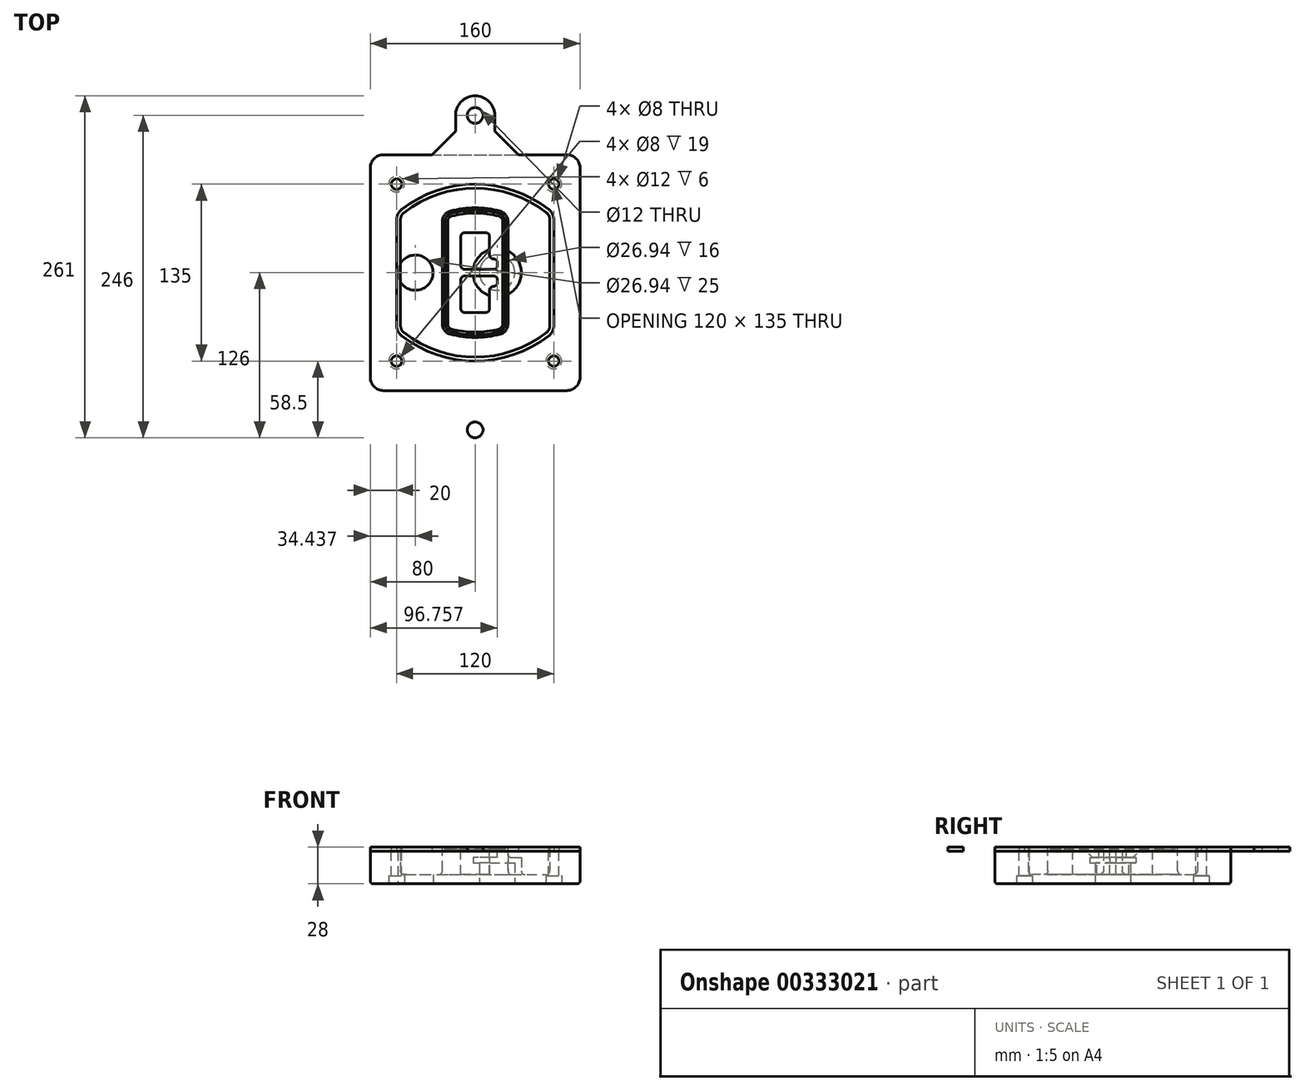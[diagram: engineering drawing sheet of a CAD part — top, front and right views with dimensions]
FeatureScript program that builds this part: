
annotation { "Feature Type Name" : "Feature", "Feature Type Description" : "" }
export const myFeature = defineFeature(function(context is Context, id is Id, definition is map)
    precondition{}
    {
        {
            var Q0;
            Q0=qCreatedBy(makeId("Top.planeOp"),FACE);
            var sketch = newSketch(context, id + "F0", { "sketchPlane" : qUnion([Q0])});
            skPoint(sketch, "E0.rect.middle", {"position": v(0, 0) * mm});
            skLineSegment(sketch, "E1.bottom", {"start": v(-70, -90) * mm, "end": v(70, -90) * mm});
            skLineSegment(sketch, "E1.top", {"start": v(-70, 90) * mm, "end": v(70, 90) * mm});
            skLineSegment(sketch, "E1.left", {"start": v(-80, -80) * mm, "end": v(-80, 80) * mm});
            skLineSegment(sketch, "E1.right", {"start": v(80, -80) * mm, "end": v(80, 80) * mm});
            skLineSegment(sketch, "E2", {"start": v(-80, 90) * mm, "end": v(80, -90) * mm, "construction": true});
            skLineSegment(sketch, "E3", {"start": v(80, 90) * mm, "end": v(-80, -90) * mm, "construction": true});
            skCircle(sketch, "E4", {"center": v(-60, 67.5) * mm, "radius": 4 * mm});
            skCircle(sketch, "E5", {"center": v(60, 67.5) * mm, "radius": 4 * mm});
            skCircle(sketch, "E6", {"center": v(60, -67.5) * mm, "radius": 4 * mm});
            skCircle(sketch, "E7", {"center": v(-60, -67.5) * mm, "radius": 4 * mm});
            skLineSegment(sketch, "E8", {"start": v(-60, 67.5) * mm, "end": v(60, 67.5) * mm, "construction": true});
            skLineSegment(sketch, "E9", {"start": v(60, 67.5) * mm, "end": v(60, -67.5) * mm, "construction": true});
            skLineSegment(sketch, "E10", {"start": v(60, -67.5) * mm, "end": v(-60, -67.5) * mm, "construction": true});
            skLineSegment(sketch, "E11", {"start": v(-60, -67.5) * mm, "end": v(-60, 67.5) * mm, "construction": true});
            skLineSegment(sketch, "E12", {"start": v(-60, 40.3) * mm, "end": v(-60, -40.3) * mm});
            skLineSegment(sketch, "E13", {"start": v(60, 40.3) * mm, "end": v(60, -40.3) * mm});
            skArc(sketch, "E14", {"start": v(56.15, 48.18) * mm, "mid": v(0, 67.5) * mm, "end": v(-56.15, 48.18) * mm});
            skArc(sketch, "E15", {"start": v(-56.15, -48.18) * mm, "mid": v(0, -67.5) * mm, "end": v(56.15, -48.18) * mm});
            skLineSegment(sketch, "E16", {"start": v(-60, 0) * mm, "end": v(60, 0) * mm, "construction": true});
            skPoint(sketch, "E17.visualSharp", {"position": v(-60, -45) * mm});
            skArc(sketch, "E17.filletArc", {"start": v(-60, -40.3) * mm, "mid": v(-58.99, -44.68) * mm, "end": v(-56.15, -48.18) * mm});
            skPoint(sketch, "E18.visualSharp", {"position": v(-60, 45) * mm});
            skArc(sketch, "E18.filletArc", {"start": v(-56.15, 48.18) * mm, "mid": v(-58.99, 44.68) * mm, "end": v(-60, 40.3) * mm});
            skPoint(sketch, "E19.visualSharp", {"position": v(60, 45) * mm});
            skArc(sketch, "E19.filletArc", {"start": v(60, 40.3) * mm, "mid": v(58.99, 44.68) * mm, "end": v(56.15, 48.18) * mm});
            skPoint(sketch, "E20.visualSharp", {"position": v(60, -45) * mm});
            skArc(sketch, "E20.filletArc", {"start": v(56.15, -48.18) * mm, "mid": v(58.99, -44.68) * mm, "end": v(60, -40.3) * mm});
            skPoint(sketch, "E21.visualSharp", {"position": v(-80, 90) * mm});
            skArc(sketch, "E21.filletArc", {"start": v(-70, 90) * mm, "mid": v(-77.07, 87.07) * mm, "end": v(-80, 80) * mm});
            skPoint(sketch, "E22.visualSharp", {"position": v(80, 90) * mm});
            skArc(sketch, "E22.filletArc", {"start": v(80, 80) * mm, "mid": v(77.07, 87.07) * mm, "end": v(70, 90) * mm});
            skPoint(sketch, "E23.visualSharp", {"position": v(80, -90) * mm});
            skArc(sketch, "E23.filletArc", {"start": v(70, -90) * mm, "mid": v(77.07, -87.07) * mm, "end": v(80, -80) * mm});
            skPoint(sketch, "E24.visualSharp", {"position": v(-80, -90) * mm});
            skArc(sketch, "E24.filletArc", {"start": v(-80, -80) * mm, "mid": v(-77.07, -87.07) * mm, "end": v(-70, -90) * mm});
            skArc(sketch, "E25.0", {"start": v(57, 40.3) * mm, "mid": v(56.3, 43.36) * mm, "end": v(54.3, 45.81) * mm});
            skLineSegment(sketch, "E25.1", {"start": v(57, 40.3) * mm, "end": v(57, -40.3) * mm});
            skArc(sketch, "E25.2", {"start": v(54.3, -45.81) * mm, "mid": v(56.3, -43.36) * mm, "end": v(57, -40.3) * mm});
            skArc(sketch, "E25.3", {"start": v(-54.3, -45.81) * mm, "mid": v(0, -64.5) * mm, "end": v(54.3, -45.81) * mm});
            skArc(sketch, "E25.4", {"start": v(-57, -40.3) * mm, "mid": v(-56.3, -43.36) * mm, "end": v(-54.3, -45.81) * mm});
            skArc(sketch, "E25.5", {"start": v(54.3, 45.81) * mm, "mid": v(0, 64.5) * mm, "end": v(-54.3, 45.81) * mm});
            skLineSegment(sketch, "E25.6", {"start": v(-57, 40.3) * mm, "end": v(-57, -40.3) * mm});
            skArc(sketch, "E25.7", {"start": v(-54.3, 45.81) * mm, "mid": v(-56.3, 43.36) * mm, "end": v(-57, 40.3) * mm});
            skArc(sketch, "E26.0", {"start": v(-58.62, 51.33) * mm, "mid": v(-62.58, 46.43) * mm, "end": v(-64, 40.3) * mm});
            skArc(sketch, "E26.1", {"start": v(58.62, 51.33) * mm, "mid": v(0, 71.5) * mm, "end": v(-58.62, 51.33) * mm});
            skArc(sketch, "E26.2", {"start": v(64, 40.3) * mm, "mid": v(62.58, 46.43) * mm, "end": v(58.62, 51.33) * mm});
            skLineSegment(sketch, "E26.3", {"start": v(64, 40.3) * mm, "end": v(64, -40.3) * mm});
            skArc(sketch, "E26.4", {"start": v(58.62, -51.33) * mm, "mid": v(62.58, -46.43) * mm, "end": v(64, -40.3) * mm});
            skLineSegment(sketch, "E26.5", {"start": v(-64, 40.3) * mm, "end": v(-64, -40.3) * mm});
            skArc(sketch, "E26.6", {"start": v(-58.62, -51.33) * mm, "mid": v(0, -71.5) * mm, "end": v(58.62, -51.33) * mm});
            skArc(sketch, "E26.7", {"start": v(-64, -40.3) * mm, "mid": v(-62.58, -46.43) * mm, "end": v(-58.62, -51.33) * mm});
            skSolve(sketch);
        }
        {
            var Q0;
            Q0=makeQuery(id+"F0.imprint","IMPRINT",FACE,{"disambiguationData":[TD([[makeQuery(id+"F0.imprint","IMPRINT",EDGE,{"derivedFrom":sQuery(id+"F0.wireOp",EDGE,"E1.bottom")}),1.0]])]});
            var Q1;
            Q1=makeQuery(id+"F0.imprint","IMPRINT",FACE,{"disambiguationData":[TD([[makeQuery(id+"F0.imprint","IMPRINT",EDGE,{"derivedFrom":sQuery(id+"F0.wireOp",EDGE,"E12")}),1.0]])]});
            var Q2;
            Q2=makeQuery(id+"F0.imprint","IMPRINT",FACE,{"disambiguationData":[TD([[makeQuery(id+"F0.imprint","IMPRINT",EDGE,{"derivedFrom":sQuery(id+"F0.wireOp",EDGE,"E25.0")}),1.0]])]});
            var Q3;
            Q3=makeQuery(id+"F0.imprint","IMPRINT",FACE,{"disambiguationData":[TD([[makeQuery(id+"F0.imprint","IMPRINT",EDGE,{"derivedFrom":sQuery(id+"F0.wireOp",EDGE,"E12")}),-1.0]])]});
            extrude(context, id + "F1", {"entities" : qUnion([Q0, Q1, Q2, Q3]), "oppositeDirection" : true, "depth" : 25 * mm});
        }
        {
            var Q0;
            Q0=makeQuery(id+"F0.imprint","IMPRINT",FACE,{"disambiguationData":[TD([[makeQuery(id+"F0.imprint","IMPRINT",EDGE,{"derivedFrom":sQuery(id+"F0.wireOp",EDGE,"E12")}),1.0]])]});
            extrude(context, id + "F2", {"entities" : qUnion([Q0]), "operationType" : NewBodyOperationType.ADD, "depth" : 3 * mm});
        }
        {
            var Q0;
            Q0=makeQuery(id+"F0.imprint","IMPRINT",FACE,{"disambiguationData":[TD([[makeQuery(id+"F0.imprint","IMPRINT",EDGE,{"derivedFrom":sQuery(id+"F0.wireOp",EDGE,"E25.0")}),1.0]])]});
            extrude(context, id + "F3", {"entities" : qUnion([Q0]), "operationType" : NewBodyOperationType.REMOVE, "oppositeDirection" : true, "depth" : 18 * mm});
        }
        {
            var Q0;
            Q0=makeQuery(id+"F2.opExtrude","CAP_FACE",FACE,{"disambiguationData":[OSD([sQuery(id+"F0.wireOp",EDGE,"E12"),sQuery(id+"F0.wireOp",EDGE,"E13"),sQuery(id+"F0.wireOp",EDGE,"E14"),sQuery(id+"F0.wireOp",EDGE,"E15"),sQuery(id+"F0.wireOp",EDGE,"E17.filletArc"),sQuery(id+"F0.wireOp",EDGE,"E18.filletArc"),sQuery(id+"F0.wireOp",EDGE,"E19.filletArc"),sQuery(id+"F0.wireOp",EDGE,"E20.filletArc"),sQuery(id+"F0.wireOp",EDGE,"E25.0"),sQuery(id+"F0.wireOp",EDGE,"E25.1"),sQuery(id+"F0.wireOp",EDGE,"E25.2"),sQuery(id+"F0.wireOp",EDGE,"E25.3"),sQuery(id+"F0.wireOp",EDGE,"E25.4"),sQuery(id+"F0.wireOp",EDGE,"E25.5"),sQuery(id+"F0.wireOp",EDGE,"E25.6"),sQuery(id+"F0.wireOp",EDGE,"E25.7")])],"isStart":false});
            var sketch = newSketch(context, id + "F4", { "sketchPlane" : qUnion([Q0])});
            skArc(sketch, "E27.0", {"start": v(-19.08, -46.97) * mm, "mid": v(0, -49.5) * mm, "end": v(19.08, -46.97) * mm});
            skArc(sketch, "E28.0", {"start": v(19.08, 46.97) * mm, "mid": v(0, 49.5) * mm, "end": v(-19.08, 46.97) * mm});
            skLineSegment(sketch, "E29", {"start": v(-25, 39.25) * mm, "end": v(-25, -39.25) * mm});
            skLineSegment(sketch, "E30", {"start": v(25, 39.25) * mm, "end": v(25, -39.25) * mm});
            skLineSegment(sketch, "E31", {"start": v(-25, 45.1) * mm, "end": v(25, 45.1) * mm, "construction": true});
            skLineSegment(sketch, "E32", {"start": v(-25, -45.1) * mm, "end": v(25, -45.1) * mm, "construction": true});
            skPoint(sketch, "E33.visualSharp", {"position": v(-25, 45.1) * mm});
            skArc(sketch, "E33.filletArc", {"start": v(-19.08, 46.97) * mm, "mid": v(-23.35, 44.11) * mm, "end": v(-25, 39.25) * mm});
            skPoint(sketch, "E34.visualSharp", {"position": v(25, 45.1) * mm});
            skArc(sketch, "E34.filletArc", {"start": v(25, 39.25) * mm, "mid": v(23.35, 44.11) * mm, "end": v(19.08, 46.97) * mm});
            skPoint(sketch, "E35.visualSharp", {"position": v(25, -45.1) * mm});
            skArc(sketch, "E35.filletArc", {"start": v(19.08, -46.97) * mm, "mid": v(23.35, -44.11) * mm, "end": v(25, -39.25) * mm});
            skPoint(sketch, "E36.visualSharp", {"position": v(-25, -45.1) * mm});
            skArc(sketch, "E36.filletArc", {"start": v(-25, -39.25) * mm, "mid": v(-23.35, -44.11) * mm, "end": v(-19.08, -46.97) * mm});
            skArc(sketch, "E37.0", {"start": v(54.3, 45.81) * mm, "mid": v(0, 64.5) * mm, "end": v(-54.3, 45.81) * mm});
            skArc(sketch, "E37.1", {"start": v(-54.3, 45.81) * mm, "mid": v(-56.3, 43.36) * mm, "end": v(-57, 40.3) * mm});
            skLineSegment(sketch, "E37.2", {"start": v(-57, 40.3) * mm, "end": v(-57, -40.3) * mm});
            skArc(sketch, "E37.3", {"start": v(-57, -40.3) * mm, "mid": v(-56.3, -43.36) * mm, "end": v(-54.3, -45.81) * mm});
            skArc(sketch, "E37.4", {"start": v(-54.3, -45.81) * mm, "mid": v(0, -64.5) * mm, "end": v(54.3, -45.81) * mm});
            skArc(sketch, "E37.5", {"start": v(54.3, -45.81) * mm, "mid": v(56.3, -43.36) * mm, "end": v(57, -40.3) * mm});
            skLineSegment(sketch, "E37.6", {"start": v(57, 40.3) * mm, "end": v(57, -40.3) * mm});
            skArc(sketch, "E37.7", {"start": v(57, 40.3) * mm, "mid": v(56.3, 43.36) * mm, "end": v(54.3, 45.81) * mm});
            skLineSegment(sketch, "E38.0", {"start": v(23, 39.25) * mm, "end": v(23, -39.25) * mm});
            skArc(sketch, "E38.1", {"start": v(18.56, -45.04) * mm, "mid": v(21.76, -42.9) * mm, "end": v(23, -39.25) * mm});
            skArc(sketch, "E38.2", {"start": v(-18.56, -45.04) * mm, "mid": v(0, -47.5) * mm, "end": v(18.56, -45.04) * mm});
            skArc(sketch, "E38.3", {"start": v(-23, -39.25) * mm, "mid": v(-21.76, -42.9) * mm, "end": v(-18.56, -45.04) * mm});
            skLineSegment(sketch, "E38.4", {"start": v(-23, 39.25) * mm, "end": v(-23, -39.25) * mm});
            skArc(sketch, "E38.5", {"start": v(23, 39.25) * mm, "mid": v(21.76, 42.9) * mm, "end": v(18.56, 45.04) * mm});
            skArc(sketch, "E38.6", {"start": v(-18.56, 45.04) * mm, "mid": v(-21.76, 42.9) * mm, "end": v(-23, 39.25) * mm});
            skArc(sketch, "E38.7", {"start": v(18.56, 45.04) * mm, "mid": v(0, 47.5) * mm, "end": v(-18.56, 45.04) * mm});
            skArc(sketch, "E39.0", {"start": v(21, 39.25) * mm, "mid": v(20.18, 41.68) * mm, "end": v(18.04, 43.1) * mm});
            skLineSegment(sketch, "E39.1", {"start": v(21, 39.25) * mm, "end": v(21, -39.25) * mm});
            skArc(sketch, "E39.2", {"start": v(18.04, -43.1) * mm, "mid": v(20.18, -41.68) * mm, "end": v(21, -39.25) * mm});
            skArc(sketch, "E39.3", {"start": v(-18.04, -43.1) * mm, "mid": v(0, -45.5) * mm, "end": v(18.04, -43.1) * mm});
            skArc(sketch, "E39.4", {"start": v(-21, -39.25) * mm, "mid": v(-20.18, -41.68) * mm, "end": v(-18.04, -43.1) * mm});
            skArc(sketch, "E39.5", {"start": v(18.04, 43.1) * mm, "mid": v(0, 45.5) * mm, "end": v(-18.04, 43.1) * mm});
            skLineSegment(sketch, "E39.6", {"start": v(-21, 39.25) * mm, "end": v(-21, -39.25) * mm});
            skArc(sketch, "E39.7", {"start": v(-18.04, 43.1) * mm, "mid": v(-20.18, 41.68) * mm, "end": v(-21, 39.25) * mm});
            skLineSegment(sketch, "E40", {"start": v(-25, 0) * mm, "end": v(25, 0) * mm, "construction": true});
            skLineSegment(sketch, "E41", {"start": v(-11, 5.5) * mm, "end": v(-11, 27.5) * mm});
            skLineSegment(sketch, "E42", {"start": v(-8, 30.5) * mm, "end": v(8, 30.5) * mm});
            skLineSegment(sketch, "E43", {"start": v(11, 27.5) * mm, "end": v(11, 13.5) * mm});
            skLineSegment(sketch, "E44", {"start": v(14, 10.5) * mm, "end": v(14, 10.5) * mm});
            skLineSegment(sketch, "E45", {"start": v(17, 7.5) * mm, "end": v(17, 5.5) * mm});
            skLineSegment(sketch, "E46", {"start": v(14, 2.5) * mm, "end": v(-8, 2.5) * mm});
            skPoint(sketch, "E47.visualSharp", {"position": v(-11, 30.5) * mm});
            skArc(sketch, "E47.filletArc", {"start": v(-8, 30.5) * mm, "mid": v(-10.12, 29.62) * mm, "end": v(-11, 27.5) * mm});
            skPoint(sketch, "E48.visualSharp", {"position": v(11, 30.5) * mm});
            skArc(sketch, "E48.filletArc", {"start": v(11, 27.5) * mm, "mid": v(10.12, 29.62) * mm, "end": v(8, 30.5) * mm});
            skPoint(sketch, "E49.visualSharp", {"position": v(11, 10.5) * mm});
            skArc(sketch, "E49.filletArc", {"start": v(11, 13.5) * mm, "mid": v(11.88, 11.38) * mm, "end": v(14, 10.5) * mm});
            skPoint(sketch, "E50.visualSharp", {"position": v(17, 10.5) * mm});
            skArc(sketch, "E50.filletArc", {"start": v(17, 7.5) * mm, "mid": v(16.12, 9.62) * mm, "end": v(14, 10.5) * mm});
            skPoint(sketch, "E51.visualSharp", {"position": v(17, 2.5) * mm});
            skArc(sketch, "E51.filletArc", {"start": v(14, 2.5) * mm, "mid": v(16.12, 3.38) * mm, "end": v(17, 5.5) * mm});
            skPoint(sketch, "E52.visualSharp", {"position": v(-11, 2.5) * mm});
            skArc(sketch, "E52.filletArc", {"start": v(-11, 5.5) * mm, "mid": v(-10.12, 3.38) * mm, "end": v(-8, 2.5) * mm});
            skLineSegment(sketch, "E53.0.MirrorCS", {"start": v(14, -2.5) * mm, "end": v(-8, -2.5) * mm});
            skArc(sketch, "E54.0.MirrorCS", {"start": v(-11, -5.5) * mm, "mid": v(-10.12, -3.38) * mm, "end": v(-8, -2.5) * mm});
            skLineSegment(sketch, "E55.0.MirrorCS", {"start": v(-11, -5.5) * mm, "end": v(-11, -27.5) * mm});
            skArc(sketch, "E56.0.MirrorCS", {"start": v(-8, -30.5) * mm, "mid": v(-10.12, -29.62) * mm, "end": v(-11, -27.5) * mm});
            skLineSegment(sketch, "E57.0.MirrorCS", {"start": v(-8, -30.5) * mm, "end": v(8, -30.5) * mm});
            skArc(sketch, "E58.0.MirrorCS", {"start": v(11, -27.5) * mm, "mid": v(10.12, -29.62) * mm, "end": v(8, -30.5) * mm});
            skLineSegment(sketch, "E59.0.MirrorCS", {"start": v(11, -27.5) * mm, "end": v(11, -13.5) * mm});
            skArc(sketch, "E60.0.MirrorCS", {"start": v(11, -13.5) * mm, "mid": v(11.88, -11.38) * mm, "end": v(14, -10.5) * mm});
            skArc(sketch, "E61.0.MirrorCS", {"start": v(17, -7.5) * mm, "mid": v(16.12, -9.62) * mm, "end": v(14, -10.5) * mm});
            skLineSegment(sketch, "E62.0.MirrorCS", {"start": v(17, -7.5) * mm, "end": v(17, -5.5) * mm});
            skArc(sketch, "E63.0.MirrorCS", {"start": v(14, -2.5) * mm, "mid": v(16.12, -3.38) * mm, "end": v(17, -5.5) * mm});
            skSolve(sketch);
        }
        {
            var Q0;
            Q0=makeQuery(id+"F4.imprint","IMPRINT",FACE,{"disambiguationData":[TD([[makeQuery(id+"F4.imprint","IMPRINT",EDGE,{"derivedFrom":sQuery(id+"F4.wireOp",EDGE,"E27.0")}),1.0]])]});
            var Q1;
            Q1=makeQuery(id+"F4.imprint","IMPRINT",FACE,{"disambiguationData":[TD([[makeQuery(id+"F4.imprint","IMPRINT",EDGE,{"derivedFrom":sQuery(id+"F4.wireOp",EDGE,"E38.0")}),-1.0]])]});
            var Q2;
            Q2=makeQuery(id+"F4.imprint","IMPRINT",FACE,{"disambiguationData":[TD([[makeQuery(id+"F4.imprint","IMPRINT",EDGE,{"derivedFrom":sQuery(id+"F4.wireOp",EDGE,"E39.0")}),1.0]])]});
            extrude(context, id + "F5", {"entities" : qUnion([Q0, Q1, Q2]), "operationType" : NewBodyOperationType.ADD, "endBound" : BoundingType.UP_TO_NEXT, "oppositeDirection" : true, "depth" : 25 * mm});
        }
        {
            var Q0;
            Q0=makeQuery(id+"F4.imprint","IMPRINT",FACE,{"disambiguationData":[TD([[makeQuery(id+"F4.imprint","IMPRINT",EDGE,{"derivedFrom":sQuery(id+"F4.wireOp",EDGE,"E38.0")}),-1.0]])]});
            extrude(context, id + "F6", {"entities" : qUnion([Q0]), "operationType" : NewBodyOperationType.REMOVE, "oppositeDirection" : true, "depth" : 2 * mm});
        }
        {
            var Q0;
            Q0=makeQuery(id+"F1.opExtrude","CAP_FACE",FACE,{"disambiguationData":[OSD([sQuery(id+"F0.wireOp",EDGE,"E1.bottom"),sQuery(id+"F0.wireOp",EDGE,"E1.top"),sQuery(id+"F0.wireOp",EDGE,"E1.left"),sQuery(id+"F0.wireOp",EDGE,"E1.right"),sQuery(id+"F0.wireOp",EDGE,"E4"),sQuery(id+"F0.wireOp",EDGE,"E5"),sQuery(id+"F0.wireOp",EDGE,"E6"),sQuery(id+"F0.wireOp",EDGE,"E7"),sQuery(id+"F0.wireOp",EDGE,"E21.filletArc"),sQuery(id+"F0.wireOp",EDGE,"E22.filletArc"),sQuery(id+"F0.wireOp",EDGE,"E23.filletArc"),sQuery(id+"F0.wireOp",EDGE,"E24.filletArc")])],"isStart":false});
            var sketch = newSketch(context, id + "F7", { "sketchPlane" : qUnion([Q0])});
            skCircle(sketch, "E64", {"center": v(16.76, 0) * mm, "radius": 13.47 * mm});
            skCircle(sketch, "E65", {"center": v(-45.56, 0) * mm, "radius": 13.47 * mm});
            skLineSegment(sketch, "E66", {"start": v(80, 0) * mm, "end": v(-80, 0) * mm});
            skCircle(sketch, "E67", {"center": v(16.76, 0) * mm, "radius": 18.47 * mm});
            skCircle(sketch, "E68", {"center": v(60, -67.5) * mm, "radius": 6 * mm});
            skCircle(sketch, "E69", {"center": v(-60, -67.5) * mm, "radius": 6 * mm});
            skCircle(sketch, "E70", {"center": v(-60, 67.5) * mm, "radius": 6 * mm});
            skCircle(sketch, "E71", {"center": v(60, 67.5) * mm, "radius": 6 * mm});
            skSolve(sketch);
        }
        {
            var Q0;
            {var subQ1=sQuery(id+"F7.wireOp",EDGE,"E66");var subQ4=sQuery(id+"F7.wireOp",EDGE,"E64");var subQ6=makeQuery(id+"F7.imprint","INTERSECT",VERTEX,{"disambiguationData":[OD(0.0)],"derivedFrom":[subQ4,subQ1]});Q0=makeQuery(id+"F7.imprint","IMPRINT",FACE,{"disambiguationData":[TD([[makeQuery(id+"F7.imprint","IMPRINT",EDGE,{"disambiguationData":[TD([[subQ6,-1.0]])],"derivedFrom":subQ4}),-1.0]])]});}
            var Q1;
            {var subQ0=sQuery(id+"F7.wireOp",EDGE,"E66");var subQ1=sQuery(id+"F7.wireOp",EDGE,"E64");var subQ3=makeQuery(id+"F7.imprint","INTERSECT",VERTEX,{"disambiguationData":[OD(0.0)],"derivedFrom":[subQ1,subQ0]});Q1=makeQuery(id+"F7.imprint","IMPRINT",FACE,{"disambiguationData":[TD([[makeQuery(id+"F7.imprint","IMPRINT",EDGE,{"disambiguationData":[TD([[subQ3,-1.0]])],"derivedFrom":subQ1}),1.0]])]});}
            var Q2;
            {var subQ0=sQuery(id+"F7.wireOp",EDGE,"E66");var subQ1=sQuery(id+"F7.wireOp",EDGE,"E64");var subQ3=makeQuery(id+"F7.imprint","INTERSECT",VERTEX,{"disambiguationData":[OD(0.0)],"derivedFrom":[subQ1,subQ0]});Q2=makeQuery(id+"F7.imprint","IMPRINT",FACE,{"disambiguationData":[TD([[makeQuery(id+"F7.imprint","IMPRINT",EDGE,{"disambiguationData":[TD([[subQ3,1.0]])],"derivedFrom":subQ1}),1.0]])]});}
            var Q3;
            {var subQ1=sQuery(id+"F7.wireOp",EDGE,"E66");var subQ4=sQuery(id+"F7.wireOp",EDGE,"E64");var subQ6=makeQuery(id+"F7.imprint","INTERSECT",VERTEX,{"disambiguationData":[OD(0.0)],"derivedFrom":[subQ4,subQ1]});Q3=makeQuery(id+"F7.imprint","IMPRINT",FACE,{"disambiguationData":[TD([[makeQuery(id+"F7.imprint","IMPRINT",EDGE,{"disambiguationData":[TD([[subQ6,1.0]])],"derivedFrom":subQ4}),-1.0]])]});}
            extrude(context, id + "F8", {"entities" : qUnion([Q0, Q1, Q2, Q3]), "operationType" : NewBodyOperationType.ADD, "oppositeDirection" : true, "depth" : 20 * mm});
        }
        {
            var Q0;
            {var subQ0=sQuery(id+"F7.wireOp",EDGE,"E66");var subQ1=sQuery(id+"F7.wireOp",EDGE,"E64");var subQ3=makeQuery(id+"F7.imprint","INTERSECT",VERTEX,{"disambiguationData":[OD(0.0)],"derivedFrom":[subQ1,subQ0]});Q0=makeQuery(id+"F7.imprint","IMPRINT",FACE,{"disambiguationData":[TD([[makeQuery(id+"F7.imprint","IMPRINT",EDGE,{"disambiguationData":[TD([[subQ3,-1.0]])],"derivedFrom":subQ1}),1.0]])]});}
            var Q1;
            {var subQ0=sQuery(id+"F7.wireOp",EDGE,"E66");var subQ1=sQuery(id+"F7.wireOp",EDGE,"E64");var subQ3=makeQuery(id+"F7.imprint","INTERSECT",VERTEX,{"disambiguationData":[OD(0.0)],"derivedFrom":[subQ1,subQ0]});Q1=makeQuery(id+"F7.imprint","IMPRINT",FACE,{"disambiguationData":[TD([[makeQuery(id+"F7.imprint","IMPRINT",EDGE,{"disambiguationData":[TD([[subQ3,1.0]])],"derivedFrom":subQ1}),1.0]])]});}
            extrude(context, id + "F9", {"entities" : qUnion([Q0, Q1]), "operationType" : NewBodyOperationType.REMOVE, "oppositeDirection" : true, "depth" : 16 * mm});
        }
        {
            var Q0;
            {var subQ0=sQuery(id+"F7.wireOp",EDGE,"E66");var subQ1=sQuery(id+"F7.wireOp",EDGE,"E65");var subQ3=makeQuery(id+"F7.imprint","INTERSECT",VERTEX,{"disambiguationData":[OD(0.0)],"derivedFrom":[subQ1,subQ0]});Q0=makeQuery(id+"F7.imprint","IMPRINT",FACE,{"disambiguationData":[TD([[makeQuery(id+"F7.imprint","IMPRINT",EDGE,{"disambiguationData":[TD([[subQ3,-1.0]])],"derivedFrom":subQ1}),1.0]])]});}
            var Q1;
            {var subQ0=sQuery(id+"F7.wireOp",EDGE,"E66");var subQ1=sQuery(id+"F7.wireOp",EDGE,"E65");var subQ3=makeQuery(id+"F7.imprint","INTERSECT",VERTEX,{"disambiguationData":[OD(0.0)],"derivedFrom":[subQ1,subQ0]});Q1=makeQuery(id+"F7.imprint","IMPRINT",FACE,{"disambiguationData":[TD([[makeQuery(id+"F7.imprint","IMPRINT",EDGE,{"disambiguationData":[TD([[subQ3,1.0]])],"derivedFrom":subQ1}),1.0]])]});}
            extrude(context, id + "F10", {"entities" : qUnion([Q0, Q1]), "operationType" : NewBodyOperationType.REMOVE, "oppositeDirection" : true, "depth" : 25 * mm});
        }
        {
            var Q0;
            Q0=makeQuery(id+"F7.imprint","IMPRINT",FACE,{"disambiguationData":[TD([[makeQuery(id+"F7.imprint","IMPRINT",EDGE,{"derivedFrom":sQuery(id+"F7.wireOp",EDGE,"E68")}),1.0]])]});
            var Q1;
            Q1=makeQuery(id+"F7.imprint","IMPRINT",FACE,{"disambiguationData":[TD([[makeQuery(id+"F7.imprint","IMPRINT",EDGE,{"derivedFrom":makeQuery(id+"F1.opExtrude","CAP_EDGE",EDGE,{"disambiguationData":[OSD([sQuery(id+"F0.wireOp",EDGE,"E5")])],"isStart":false})}),-1.0]])]});
            var Q2;
            Q2=makeQuery(id+"F7.imprint","IMPRINT",FACE,{"disambiguationData":[TD([[makeQuery(id+"F7.imprint","IMPRINT",EDGE,{"derivedFrom":sQuery(id+"F7.wireOp",EDGE,"E69")}),1.0]])]});
            var Q3;
            Q3=makeQuery(id+"F7.imprint","IMPRINT",FACE,{"disambiguationData":[TD([[makeQuery(id+"F7.imprint","IMPRINT",EDGE,{"derivedFrom":makeQuery(id+"F1.opExtrude","CAP_EDGE",EDGE,{"disambiguationData":[OSD([sQuery(id+"F0.wireOp",EDGE,"E4")])],"isStart":false})}),-1.0]])]});
            var Q4;
            Q4=makeQuery(id+"F7.imprint","IMPRINT",FACE,{"disambiguationData":[TD([[makeQuery(id+"F7.imprint","IMPRINT",EDGE,{"derivedFrom":sQuery(id+"F7.wireOp",EDGE,"E70")}),1.0]])]});
            var Q5;
            Q5=makeQuery(id+"F7.imprint","IMPRINT",FACE,{"disambiguationData":[TD([[makeQuery(id+"F7.imprint","IMPRINT",EDGE,{"derivedFrom":makeQuery(id+"F1.opExtrude","CAP_EDGE",EDGE,{"disambiguationData":[OSD([sQuery(id+"F0.wireOp",EDGE,"E7")])],"isStart":false})}),-1.0]])]});
            var Q6;
            Q6=makeQuery(id+"F7.imprint","IMPRINT",FACE,{"disambiguationData":[TD([[makeQuery(id+"F7.imprint","IMPRINT",EDGE,{"derivedFrom":sQuery(id+"F7.wireOp",EDGE,"E71")}),1.0]])]});
            var Q7;
            Q7=makeQuery(id+"F7.imprint","IMPRINT",FACE,{"disambiguationData":[TD([[makeQuery(id+"F7.imprint","IMPRINT",EDGE,{"derivedFrom":makeQuery(id+"F1.opExtrude","CAP_EDGE",EDGE,{"disambiguationData":[OSD([sQuery(id+"F0.wireOp",EDGE,"E6")])],"isStart":false})}),-1.0]])]});
            extrude(context, id + "F11", {"entities" : qUnion([Q0, Q1, Q2, Q3, Q4, Q5, Q6, Q7]), "operationType" : NewBodyOperationType.REMOVE, "oppositeDirection" : true, "depth" : 6 * mm});
        }
        {
            var Q0;
            Q0=makeQuery(id+"F9.boolean.opBoolean","COPY",FACE,{"derivedFrom":makeQuery(id+"F9.opExtrude","CAP_FACE",FACE,{"disambiguationData":[OSD([sQuery(id+"F7.wireOp",EDGE,"E64")])],"isStart":false})});
            var sketch = newSketch(context, id + "F12", { "sketchPlane" : qUnion([Q0])});
            skArc(sketch, "E72.0", {"start": v(11, 17.55) * mm, "mid": v(2.57, 11.82) * mm, "end": v(-1.54, 2.5) * mm});
            skArc(sketch, "E72.1", {"start": v(-1.54, -2.5) * mm, "mid": v(2.57, -11.82) * mm, "end": v(11, -17.55) * mm});
            skLineSegment(sketch, "E73", {"start": v(-1.54, -2.5) * mm, "end": v(14, -2.5) * mm});
            skLineSegment(sketch, "E74.0", {"start": v(14, 2.5) * mm, "end": v(-1.54, 2.5) * mm});
            skArc(sketch, "E74.1", {"start": v(14, 2.5) * mm, "mid": v(16.12, 3.38) * mm, "end": v(17, 5.5) * mm});
            skLineSegment(sketch, "E74.2", {"start": v(17, 7.5) * mm, "end": v(17, 5.5) * mm});
            skArc(sketch, "E74.3", {"start": v(17, 7.5) * mm, "mid": v(16.12, 9.62) * mm, "end": v(14, 10.5) * mm});
            skArc(sketch, "E74.4", {"start": v(11, 13.5) * mm, "mid": v(11.88, 11.38) * mm, "end": v(14, 10.5) * mm});
            skLineSegment(sketch, "E74.5", {"start": v(11, 17.55) * mm, "end": v(11, 13.5) * mm});
            skLineSegment(sketch, "E74.7", {"start": v(14, -2.5) * mm, "end": v(-1.54, -2.5) * mm});
            skArc(sketch, "E74.8", {"start": v(14, -2.5) * mm, "mid": v(16.12, -3.38) * mm, "end": v(17, -5.5) * mm});
            skLineSegment(sketch, "E74.9", {"start": v(17, -7.5) * mm, "end": v(17, -5.5) * mm});
            skArc(sketch, "E74.10", {"start": v(17, -7.5) * mm, "mid": v(16.12, -9.62) * mm, "end": v(14, -10.5) * mm});
            skArc(sketch, "E74.11", {"start": v(11, -13.5) * mm, "mid": v(11.88, -11.38) * mm, "end": v(14, -10.5) * mm});
            skLineSegment(sketch, "E74.12", {"start": v(11, -17.55) * mm, "end": v(11, -13.5) * mm});
            skPoint(sketch, "E75.orphan", {"position": v(11, -27.5) * mm});
            skPoint(sketch, "E76.orphan", {"position": v(-8, -2.5) * mm});
            skPoint(sketch, "E77.orphan", {"position": v(-8, 2.5) * mm});
            skPoint(sketch, "E78.orphan", {"position": v(11, 27.5) * mm});
            skSolve(sketch);
        }
        {
            var Q0;
            {var subQ7=sQuery(id+"F12.wireOp",EDGE,"E72.0");var subQ14=sQuery(id+"F12.wireOp",EDGE,"E72.1");var subQ16=sQuery(id+"F12.wireOp",EDGE,"E74.1");var subQ18=sQuery(id+"F12.wireOp",EDGE,"E74.8");Q0=qUnion([makeQuery(id+"F12.imprint","IMPRINT",FACE,{"disambiguationData":[TD([[makeQuery(id+"F12.imprint","IMPRINT",EDGE,{"derivedFrom":subQ7}),1.0]])]}),makeQuery(id+"F12.imprint","IMPRINT",FACE,{"disambiguationData":[TD([[makeQuery(id+"F12.imprint","IMPRINT",EDGE,{"derivedFrom":subQ14}),1.0]])]}),makeQuery(id+"F12.imprint","IMPRINT",FACE,{"disambiguationData":[TD([[makeQuery(id+"F12.imprint","IMPRINT",EDGE,{"derivedFrom":subQ16}),1.0]])]}),makeQuery(id+"F12.imprint","IMPRINT",FACE,{"disambiguationData":[TD([[makeQuery(id+"F12.imprint","IMPRINT",EDGE,{"derivedFrom":subQ18}),-1.0]])]})]);}
            var Q1;
            Q1=makeQuery(id+"F5.boolean.opBoolean","SPLIT",FACE,{"disambiguationData":[TD([makeQuery(id+"F5.opExtrude","SWEPT_FACE",FACE,{"disambiguationData":[OSD([sQuery(id+"F4.wireOp",EDGE,"E41")])]})])],"derivedFrom":makeQuery(id+"F3.boolean.opBoolean","COPY",FACE,{"derivedFrom":makeQuery(id+"F3.opExtrude","CAP_FACE",FACE,{"disambiguationData":[OSD([sQuery(id+"F0.wireOp",EDGE,"E25.0"),sQuery(id+"F0.wireOp",EDGE,"E25.1"),sQuery(id+"F0.wireOp",EDGE,"E25.2"),sQuery(id+"F0.wireOp",EDGE,"E25.3"),sQuery(id+"F0.wireOp",EDGE,"E25.4"),sQuery(id+"F0.wireOp",EDGE,"E25.5"),sQuery(id+"F0.wireOp",EDGE,"E25.6"),sQuery(id+"F0.wireOp",EDGE,"E25.7")])],"isStart":false})})});
            extrude(context, id + "F13", {"entities" : qUnion([Q0]), "operationType" : NewBodyOperationType.REMOVE, "endBound" : BoundingType.UP_TO_SURFACE, "endBoundEntityFace" : qUnion([Q1]), "depth" : 25 * mm});
        }
        {
            var Q0;
            Q0=makeQuery(id+"F3.boolean.opBoolean","COPY",EDGE,{"derivedFrom":makeQuery(id+"F3.opExtrude","CAP_EDGE",EDGE,{"disambiguationData":[OSD([sQuery(id+"F0.wireOp",EDGE,"E25.6")])],"isStart":false})});
            var Q1;
            Q1=makeQuery(id+"F8.boolean.opBoolean","INTERSECT",EDGE,{"derivedFrom":[makeQuery(id+"F5.opExtrude","SWEPT_FACE",FACE,{"disambiguationData":[OSD([sQuery(id+"F4.wireOp",EDGE,"E30")])]}),makeQuery(id+"F8.opExtrude","CAP_FACE",FACE,{"disambiguationData":[OSD([sQuery(id+"F7.wireOp",EDGE,"E67")])],"isStart":false})]});
            var Q2;
            Q2=makeQuery(id+"F8.boolean.opBoolean","INTERSECT",EDGE,{"disambiguationData":[OD(1.0)],"derivedFrom":[makeQuery(id+"F5.opExtrude","SWEPT_FACE",FACE,{"disambiguationData":[OSD([sQuery(id+"F4.wireOp",EDGE,"E30")])]}),makeQuery(id+"F8.opExtrude","SWEPT_FACE",FACE,{"disambiguationData":[OSD([sQuery(id+"F7.wireOp",EDGE,"E67")])]})]});
            var Q3;
            {var subQ0=sQuery(id+"F4.wireOp",EDGE,"E30");Q3=makeQuery(id+"F8.boolean.opBoolean","SPLIT",EDGE,{"disambiguationData":[TD([makeQuery(id+"F5.opExtrude","SWEPT_FACE",FACE,{"disambiguationData":[OSD([sQuery(id+"F4.wireOp",EDGE,"E35.filletArc")])]})])],"derivedFrom":makeQuery(id+"F5.opExtrude","CAP_EDGE",EDGE,{"disambiguationData":[OSD([subQ0])],"isStart":false})});}
            var Q4;
            {var subQ0=sQuery(id+"F0.wireOp",EDGE,"E25.7");var subQ1=sQuery(id+"F0.wireOp",EDGE,"E25.1");var subQ2=sQuery(id+"F0.wireOp",EDGE,"E25.6");var subQ3=sQuery(id+"F0.wireOp",EDGE,"E25.5");var subQ4=sQuery(id+"F0.wireOp",EDGE,"E25.4");var subQ5=sQuery(id+"F0.wireOp",EDGE,"E25.0");var subQ6=sQuery(id+"F0.wireOp",EDGE,"E25.2");var subQ7=sQuery(id+"F0.wireOp",EDGE,"E25.3");Q4=makeQuery(id+"F8.boolean.opBoolean","INTERSECT",EDGE,{"derivedFrom":[makeQuery(id+"F5.boolean.opBoolean","SPLIT",FACE,{"disambiguationData":[TD([makeQuery(id+"F2.opExtrude","SWEPT_FACE",FACE,{"disambiguationData":[OSD([subQ5])]})])],"derivedFrom":makeQuery(id+"F3.boolean.opBoolean","COPY",FACE,{"derivedFrom":makeQuery(id+"F3.opExtrude","CAP_FACE",FACE,{"disambiguationData":[OSD([subQ5,subQ1,subQ6,subQ7,subQ4,subQ3,subQ2,subQ0])],"isStart":false})})}),makeQuery(id+"F8.opExtrude","SWEPT_FACE",FACE,{"disambiguationData":[OSD([sQuery(id+"F7.wireOp",EDGE,"E67")])]})]});}
            var Q5;
            Q5=makeQuery(id+"F8.boolean.opBoolean","INTERSECT",EDGE,{"disambiguationData":[OD(0.0)],"derivedFrom":[makeQuery(id+"F5.opExtrude","SWEPT_FACE",FACE,{"disambiguationData":[OSD([sQuery(id+"F4.wireOp",EDGE,"E30")])]}),makeQuery(id+"F8.opExtrude","SWEPT_FACE",FACE,{"disambiguationData":[OSD([sQuery(id+"F7.wireOp",EDGE,"E67")])]})]});
            fillet(context, id + "F14", {"entities" : qUnion([Q0, Q1, Q2, Q3, Q4, Q5]), "radius" : 3 * mm, "tangentPropagation" : true, "allowEdgeOverflow" : false});
        }
        {
            var Q0;
            Q0=makeQuery(id+"F1.opExtrude","CAP_EDGE",EDGE,{"disambiguationData":[OSD([sQuery(id+"F0.wireOp",EDGE,"E1.bottom")])],"isStart":false});
            fillet(context, id + "F15", {"entities" : qUnion([Q0]), "radius" : 2 * mm, "tangentPropagation" : true, "allowEdgeOverflow" : false});
        }
        {
            var Q0;
            {var subQ0=sQuery(id+"F0.wireOp",EDGE,"E21.filletArc");var subQ1=sQuery(id+"F0.wireOp",EDGE,"E7");var subQ2=sQuery(id+"F0.wireOp",EDGE,"E6");var subQ3=sQuery(id+"F0.wireOp",EDGE,"E5");var subQ4=sQuery(id+"F0.wireOp",EDGE,"E4");var subQ5=sQuery(id+"F0.wireOp",EDGE,"E22.filletArc");var subQ6=sQuery(id+"F0.wireOp",EDGE,"E1.bottom");var subQ7=sQuery(id+"F0.wireOp",EDGE,"E1.right");var subQ8=sQuery(id+"F0.wireOp",EDGE,"E1.top");var subQ9=sQuery(id+"F0.wireOp",EDGE,"E1.left");var subQ10=sQuery(id+"F0.wireOp",EDGE,"E23.filletArc");var subQ11=sQuery(id+"F0.wireOp",EDGE,"E24.filletArc");Q0=makeQuery(id+"F2.boolean.opBoolean","SPLIT",FACE,{"disambiguationData":[TD([makeQuery(id+"F1.opExtrude","SWEPT_FACE",FACE,{"disambiguationData":[OSD([subQ6])]})])],"derivedFrom":makeQuery(id+"F1.opExtrude","CAP_FACE",FACE,{"disambiguationData":[OSD([subQ6,subQ8,subQ9,subQ7,subQ4,subQ3,subQ2,subQ1,subQ0,subQ5,subQ10,subQ11])],"isStart":true})});}
            var sketch = newSketch(context, id + "F16", { "sketchPlane" : qUnion([Q0])});
            skLineSegment(sketch, "E79", {"start": v(0, 90) * mm, "end": v(0, 120) * mm, "construction": true});
            skCircle(sketch, "E80", {"center": v(0, 120) * mm, "radius": 6 * mm});
            skLineSegment(sketch, "E81", {"start": v(33, 90) * mm, "end": v(15, 108) * mm});
            skLineSegment(sketch, "E82", {"start": v(15, 108) * mm, "end": v(15, 120) * mm});
            skLineSegment(sketch, "E83", {"start": v(-33, 90) * mm, "end": v(-15, 108) * mm});
            skLineSegment(sketch, "E84", {"start": v(-15, 108) * mm, "end": v(-15, 120) * mm});
            skArc(sketch, "E85", {"start": v(15, 120) * mm, "mid": v(0, 135) * mm, "end": v(-15, 120) * mm});
            skLineSegment(sketch, "E86", {"start": v(-80, 0) * mm, "end": v(80, 0) * mm, "construction": true});
            skLineSegment(sketch, "E87.MirrorCS", {"start": v(33, -90) * mm, "end": v(15, -108) * mm});
            skLineSegment(sketch, "E88.MirrorCS", {"start": v(15, -108) * mm, "end": v(15, -120) * mm});
            skArc(sketch, "E89.MirrorCS", {"start": v(15, -120) * mm, "mid": v(0, -135) * mm, "end": v(-15, -120) * mm});
            skCircle(sketch, "E90.MirrorC", {"center": v(0, -120) * mm, "radius": 6 * mm});
            skLineSegment(sketch, "E91.MirrorCS", {"start": v(-15, -108) * mm, "end": v(-15, -120) * mm});
            skLineSegment(sketch, "E92.MirrorCS", {"start": v(-33, -90) * mm, "end": v(-15, -108) * mm});
            skLineSegment(sketch, "E93.MirrorCS", {"start": v(0, -90) * mm, "end": v(0, -120) * mm, "construction": true});
            skSolve(sketch);
        }
        {
            var Q0;
            Q0=makeQuery(id+"F16.imprint","IMPRINT",FACE,{"disambiguationData":[TD([[makeQuery(id+"F16.imprint","IMPRINT",EDGE,{"derivedFrom":sQuery(id+"F16.wireOp",EDGE,"E80")}),-1.0]])]});
            var Q1;
            Q1=makeQuery(id+"F16.imprint","IMPRINT",FACE,{"disambiguationData":[TD([[makeQuery(id+"F16.imprint","IMPRINT",EDGE,{"derivedFrom":makeQuery(id+"F1.opExtrude","CAP_EDGE",EDGE,{"disambiguationData":[OSD([sQuery(id+"F0.wireOp",EDGE,"E1.left")])],"isStart":true})}),-1.0]])]});
            var Q2;
            Q2=makeQuery(id+"F16.imprint","IMPRINT",FACE,{"disambiguationData":[TD([[makeQuery(id+"F16.imprint","IMPRINT",EDGE,{"derivedFrom":sQuery(id+"F16.wireOp",EDGE,"E90.MirrorC")}),1.0]])]});
            var Q3;
            Q3=makeQuery(id+"F2.opExtrude","CAP_FACE",FACE,{"disambiguationData":[OSD([sQuery(id+"F0.wireOp",EDGE,"E12"),sQuery(id+"F0.wireOp",EDGE,"E13"),sQuery(id+"F0.wireOp",EDGE,"E14"),sQuery(id+"F0.wireOp",EDGE,"E15"),sQuery(id+"F0.wireOp",EDGE,"E17.filletArc"),sQuery(id+"F0.wireOp",EDGE,"E18.filletArc"),sQuery(id+"F0.wireOp",EDGE,"E19.filletArc"),sQuery(id+"F0.wireOp",EDGE,"E20.filletArc"),sQuery(id+"F0.wireOp",EDGE,"E25.0"),sQuery(id+"F0.wireOp",EDGE,"E25.1"),sQuery(id+"F0.wireOp",EDGE,"E25.2"),sQuery(id+"F0.wireOp",EDGE,"E25.3"),sQuery(id+"F0.wireOp",EDGE,"E25.4"),sQuery(id+"F0.wireOp",EDGE,"E25.5"),sQuery(id+"F0.wireOp",EDGE,"E25.6"),sQuery(id+"F0.wireOp",EDGE,"E25.7")])],"isStart":false});
            extrude(context, id + "F17", {"entities" : qUnion([Q0, Q1, Q2]), "endBound" : BoundingType.UP_TO_SURFACE, "endBoundEntityFace" : qUnion([Q3]), "depth" : 25 * mm});
        }
    });
